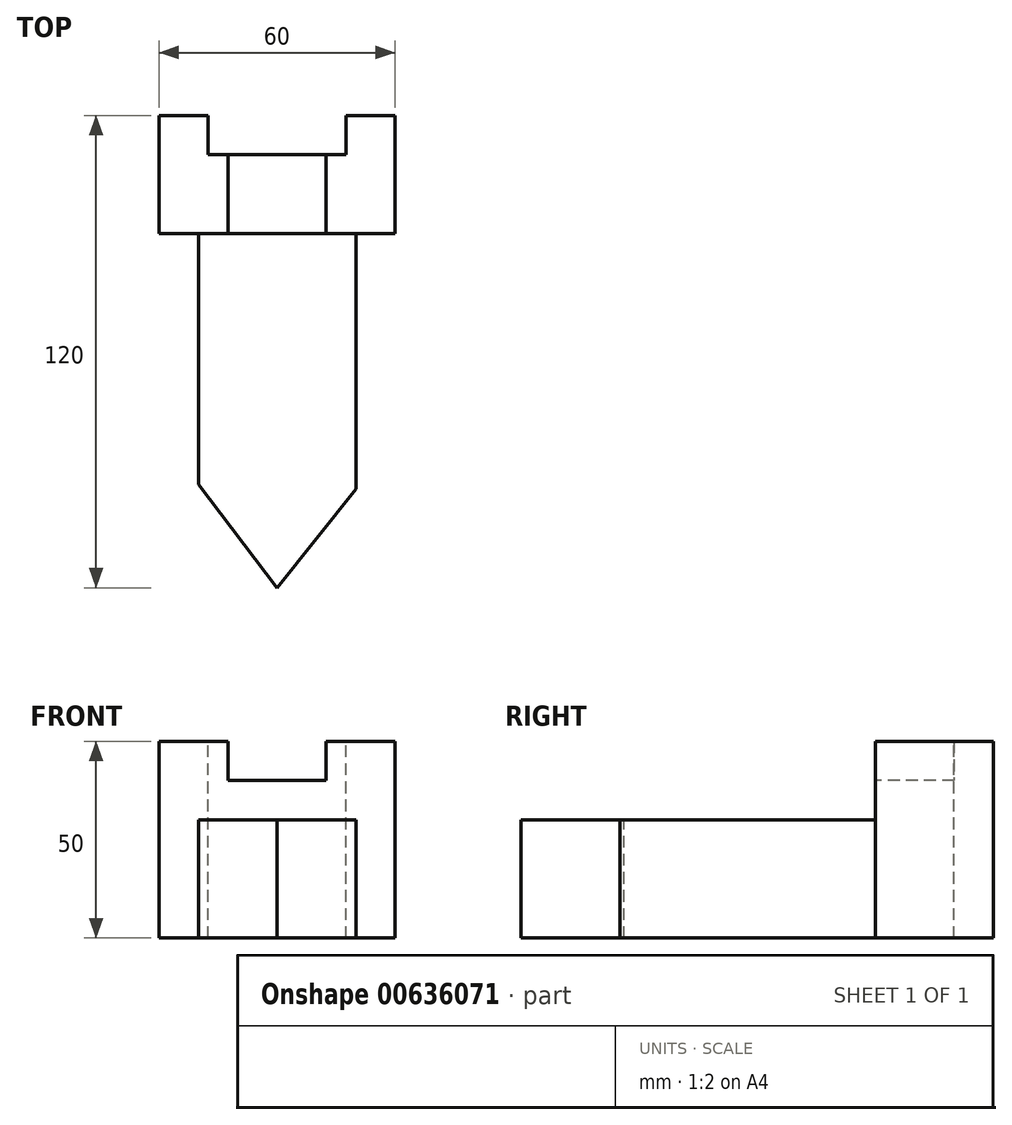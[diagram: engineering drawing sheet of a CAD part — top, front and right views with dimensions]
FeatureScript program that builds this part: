
annotation { "Feature Type Name" : "Feature", "Feature Type Description" : "" }
export const myFeature = defineFeature(function(context is Context, id is Id, definition is map)
    precondition{}
    {
        {
            var Q0;
            Q0=qCreatedBy(makeId("Front.planeOp"),FACE);
            var sketch = newSketch(context, id + "F0", { "sketchPlane" : qUnion([Q0])});
            skLineSegment(sketch, "E0.bottom", {"start": v(-30, 25) * mm, "end": v(30, 25) * mm});
            skLineSegment(sketch, "E0.top", {"start": v(-30, -25) * mm, "end": v(30, -25) * mm});
            skLineSegment(sketch, "E0.left", {"start": v(-30, 25) * mm, "end": v(-30, -25) * mm});
            skLineSegment(sketch, "E0.right", {"start": v(30, 25) * mm, "end": v(30, -25) * mm});
            skPoint(sketch, "E0.middle", {"position": v(0, 0) * mm});
            skSolve(sketch);
        }
        {
            var Q0;
            Q0 = qSketchRegion(id + "F0", true);
            extrude(context, id + "F1", {"entities" : qUnion([Q0]), "depth" : 30 * mm, "offsetDistance" : 25 * mm});
        }
        {
            var Q0;
            Q0=makeQuery(id+"F1.opExtrude","CAP_FACE",FACE,{"disambiguationData":[OSD([sQuery(id+"F0.wireOp",EDGE,"E0.bottom"),sQuery(id+"F0.wireOp",EDGE,"E0.top"),sQuery(id+"F0.wireOp",EDGE,"E0.left"),sQuery(id+"F0.wireOp",EDGE,"E0.right")])],"isStart":false});
            var sketch = newSketch(context, id + "F2", { "sketchPlane" : qUnion([Q0])});
            skLineSegment(sketch, "E1", {"start": v(-12.5, 25) * mm, "end": v(-12.5, 15) * mm});
            skLineSegment(sketch, "E2", {"start": v(-12.5, 15) * mm, "end": v(12.5, 15) * mm});
            skLineSegment(sketch, "E3", {"start": v(12.5, 15) * mm, "end": v(12.5, 25) * mm});
            skSolve(sketch);
        }
        {
            var Q0;
            Q0 = qSketchRegion(id + "F2", true);
            var Q1;
            {var subQ0=sQuery(id+"F2.wireOp",EDGE,"E1");Q1=makeQuery(id+"F2.imprint","IMPRINT",FACE,{"disambiguationData":[TD([[makeQuery(id+"F2.imprint","IMPRINT",EDGE,{"derivedFrom":subQ0}),1.0]])]});}
            extrude(context, id + "F3", {"entities" : qUnion([Q0, Q1]), "operationType" : NewBodyOperationType.REMOVE, "endBound" : BoundingType.THROUGH_ALL, "oppositeDirection" : true, "depth" : 25 * mm, "offsetDistance" : 25 * mm});
        }
        {
            var Q0;
            Q0=makeQuery(id+"F3.boolean.opBoolean","COPY",FACE,{"derivedFrom":makeQuery(id+"F3.opExtrude","SWEPT_FACE",FACE,{"disambiguationData":[OSD([sQuery(id+"F2.wireOp",EDGE,"E2")])]})});
            var sketch = newSketch(context, id + "F4", { "sketchPlane" : qUnion([Q0])});
            skLineSegment(sketch, "E4", {"start": v(-12.5, -10) * mm, "end": v(-17.5, -10) * mm});
            skLineSegment(sketch, "E5", {"start": v(-17.5, -10) * mm, "end": v(-17.5, 0) * mm});
            skLineSegment(sketch, "E6", {"start": v(-17.5, 0) * mm, "end": v(17.5, 0) * mm});
            skLineSegment(sketch, "E7", {"start": v(17.5, 0) * mm, "end": v(17.5, -10) * mm});
            skLineSegment(sketch, "E8", {"start": v(17.5, -10) * mm, "end": v(-12.5, -10) * mm});
            skSolve(sketch);
        }
        {
            var Q0;
            Q0 = qSketchRegion(id + "F4", true);
            extrude(context, id + "F5", {"entities" : qUnion([Q0]), "operationType" : NewBodyOperationType.REMOVE, "endBound" : BoundingType.THROUGH_ALL, "oppositeDirection" : true, "depth" : 25 * mm, "offsetDistance" : 25 * mm});
        }
        {
            var Q0;
            {var subQ0=sQuery(id+"F4.wireOp",EDGE,"E8");var subQ1=sQuery(id+"F4.wireOp",EDGE,"E4");var subQ2=sQuery(id+"F4.wireOp",EDGE,"E7");Q0=makeQuery(id+"F5.boolean.opBoolean","COPY",FACE,{"disambiguationData":[TD([makeQuery(id+"F3.boolean.opBoolean","COPY",FACE,{"derivedFrom":makeQuery(id+"F3.opExtrude","SWEPT_FACE",FACE,{"disambiguationData":[OSD([sQuery(id+"F2.wireOp",EDGE,"E3")])]})})])],"derivedFrom":makeQuery(id+"F5.opExtrude","CAP_FACE",FACE,{"disambiguationData":[OSD([subQ1,sQuery(id+"F4.wireOp",EDGE,"E5"),sQuery(id+"F4.wireOp",EDGE,"E6"),subQ2,subQ0])],"isStart":true})});}
            var Q1;
            {var subQ0=sQuery(id+"F4.wireOp",EDGE,"E8");var subQ1=sQuery(id+"F4.wireOp",EDGE,"E4");var subQ2=sQuery(id+"F4.wireOp",EDGE,"E5");Q1=makeQuery(id+"F5.boolean.opBoolean","COPY",FACE,{"disambiguationData":[TD([makeQuery(id+"F3.boolean.opBoolean","COPY",FACE,{"derivedFrom":makeQuery(id+"F3.opExtrude","SWEPT_FACE",FACE,{"disambiguationData":[OSD([sQuery(id+"F2.wireOp",EDGE,"E1")])]})})])],"derivedFrom":makeQuery(id+"F5.opExtrude","CAP_FACE",FACE,{"disambiguationData":[OSD([subQ1,subQ2,sQuery(id+"F4.wireOp",EDGE,"E6"),sQuery(id+"F4.wireOp",EDGE,"E7"),subQ0])],"isStart":true})});}
            extrude(context, id + "F6", {"entities" : qUnion([Q0, Q1]), "operationType" : NewBodyOperationType.REMOVE, "endBound" : BoundingType.THROUGH_ALL, "oppositeDirection" : true, "depth" : 25 * mm, "offsetDistance" : 25 * mm});
        }
        {
            var Q0;
            Q0=makeQuery(id+"F3.boolean.opBoolean","COPY",FACE,{"derivedFrom":makeQuery(id+"F3.opExtrude","SWEPT_FACE",FACE,{"disambiguationData":[OSD([sQuery(id+"F2.wireOp",EDGE,"E2")])]})});
            cPlane(context, id + "F7", {"entities" : qUnion([Q0]), "cplaneType" : CPlaneType.OFFSET, "offset" : 10 * mm, "oppositeDirection" : true, "width" : 150 * mm, "height" : 150 * mm});
        }
        {
            var Q0;
            Q0=qCreatedBy(id+"F7.planeOp",FACE);
            var sketch = newSketch(context, id + "F8", { "sketchPlane" : qUnion([Q0])});
            skLineSegment(sketch, "E9", {"start": v(-62.9, -1737.65) * mm, "end": v(-62.9, -1827.65) * mm});
            skLineSegment(sketch, "E10", {"start": v(-62.9, -1827.65) * mm, "end": v(-22.9, -1827.65) * mm});
            skLineSegment(sketch, "E11", {"start": v(-20, -30) * mm, "end": v(-20, -120) * mm});
            skLineSegment(sketch, "E12", {"start": v(-20, -120) * mm, "end": v(20, -120) * mm});
            skLineSegment(sketch, "E13", {"start": v(20.05, -30) * mm, "end": v(20, -120) * mm});
            skLineSegment(sketch, "E14", {"start": v(-20, -30) * mm, "end": v(20.05, -30) * mm});
            skSolve(sketch);
        }
        {
            var Q0;
            Q0 = qSketchRegion(id + "F8", true);
            extrude(context, id + "F9", {"entities" : qUnion([Q0]), "operationType" : NewBodyOperationType.ADD, "oppositeDirection" : true, "depth" : 30 * mm, "offsetDistance" : 25 * mm});
        }
        {
            var Q0;
            Q0=makeQuery(id+"F9.opExtrude","CAP_FACE",FACE,{"disambiguationData":[OSD([sQuery(id+"F8.wireOp",EDGE,"E11"),sQuery(id+"F8.wireOp",EDGE,"E12"),sQuery(id+"F8.wireOp",EDGE,"E13"),sQuery(id+"F8.wireOp",EDGE,"E14")])],"isStart":true});
            var sketch = newSketch(context, id + "F10", { "sketchPlane" : qUnion([Q0])});
            skLineSegment(sketch, "E15", {"start": v(-20, -93.82) * mm, "end": v(0, -120) * mm});
            skLineSegment(sketch, "E16", {"start": v(0, -8.74) * mm, "end": v(0, -136.74) * mm, "construction": true});
            skPoint(sketch, "E16.startSnap0", {"position": v(0, -120) * mm});
            skLineSegment(sketch, "E17", {"start": v(0, -120) * mm, "end": v(-20, -120) * mm});
            skLineSegment(sketch, "E18", {"start": v(-20, -120) * mm, "end": v(-20, -93.82) * mm});
            skLineSegment(sketch, "E19.MirrorCS", {"start": v(0, -120) * mm, "end": v(20, -120) * mm});
            skLineSegment(sketch, "E20", {"start": v(0, -120) * mm, "end": v(20.01, -94.92) * mm});
            skLineSegment(sketch, "E21", {"start": v(20.01, -94.92) * mm, "end": v(20, -120) * mm});
            skSolve(sketch);
        }
        {
            var Q0;
            Q0 = qSketchRegion(id + "F10", true);
            extrude(context, id + "F11", {"entities" : qUnion([Q0]), "operationType" : NewBodyOperationType.REMOVE, "endBound" : BoundingType.THROUGH_ALL, "oppositeDirection" : true, "depth" : 25 * mm, "offsetDistance" : 25 * mm});
        }
    });
